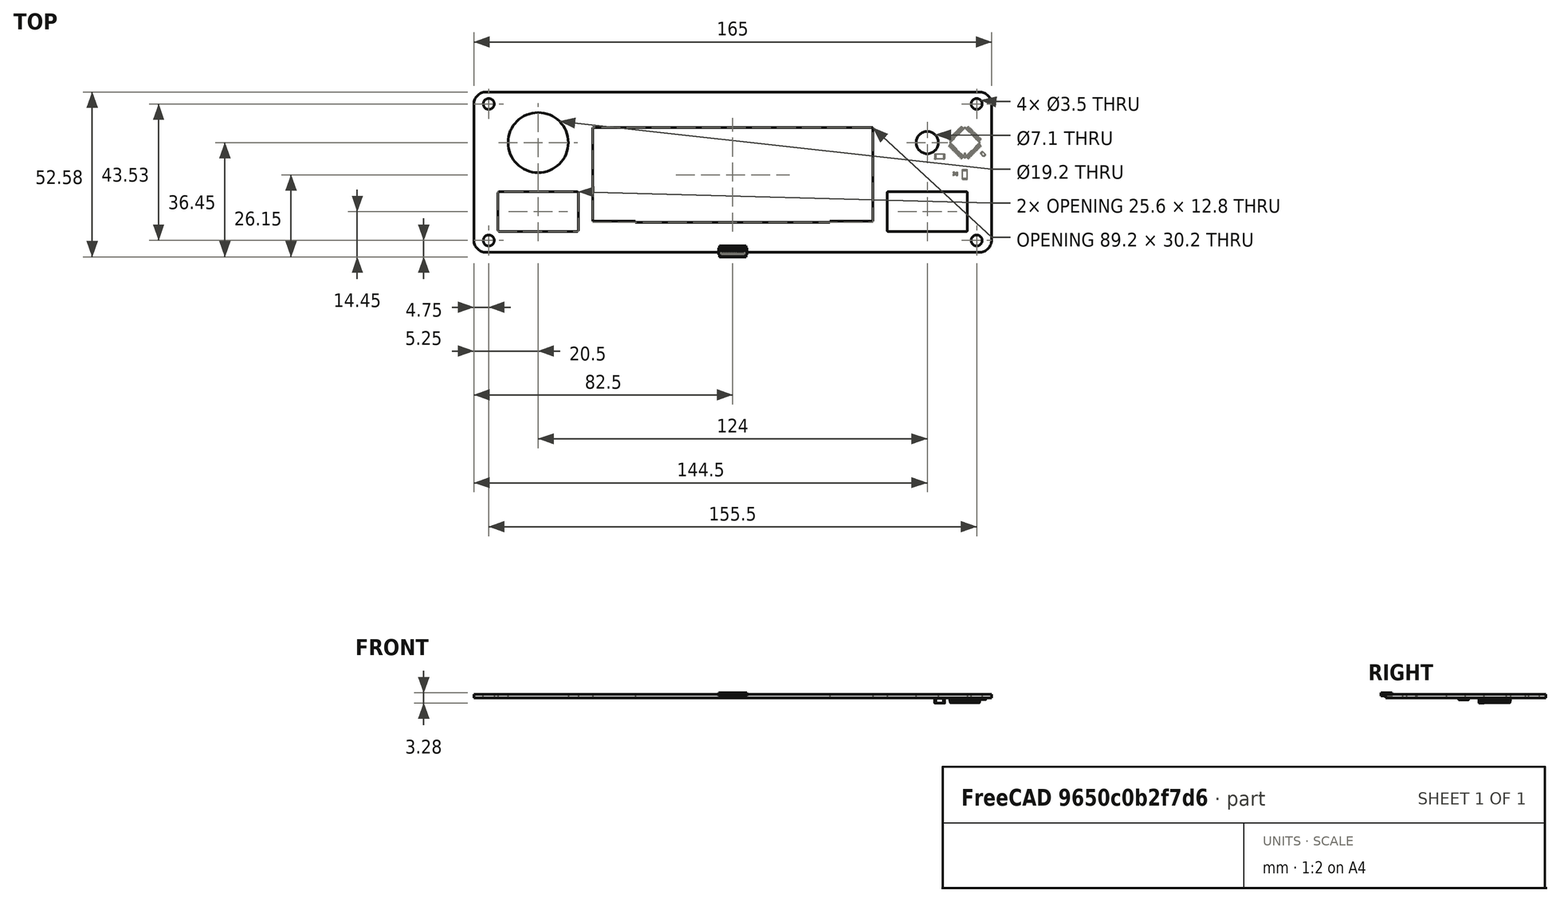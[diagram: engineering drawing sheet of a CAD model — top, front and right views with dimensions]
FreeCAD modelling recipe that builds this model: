
FCSTD DOCUMENT  (FreeCAD 0.19R)
Label: ss_frontpanel_outer_plate-3d
License: All rights reserved
LicenseURL: http://en.wikipedia.org/wiki/All_rights_reserved
objects: App::Link×30, Part::Feature×27, App::Part×5, PartDesign::CoordinateSystem×1, Sketcher::SketchObject×1
note: 29 computed .brp shape members not serialized (recipe doc carries the construction recipe); baked Part::Feature solids carry a one-line shape summary decoded from their .brp

FEATURE [PartDesign::CoordinateSystem] Local_CS_ea1d
  AttacherType = Attacher::AttachEngine3D
FEATURE [Part::Feature] Pcb_ea1d
  Placement = pos=(-150,100,0) rot=(0,0,1;0rad)
  shape: bbox 165 x 51.13 x 1.2 mm, 40 faces (baked)
FEATURE [Sketcher::SketchObject] PCB_Sketch_ea1d
  FullyConstrained = false
  sketch-geometry (8):
    g0: LineSegment StartX=-78.61 StartY=51.13 StartZ=0 EndX=78.61 EndY=51.13 EndZ=0
    g1: LineSegment StartX=82.5 StartY=47.24 StartZ=0 EndX=82.5 EndY=3.89 EndZ=0
    g2: LineSegment StartX=78.61 StartY=1.3e-15 StartZ=0 EndX=-78.61 EndY=-5.3e-15 EndZ=0
    g3: LineSegment StartX=-82.5 StartY=3.89 StartZ=0 EndX=-82.5 EndY=47.24 EndZ=0
    g4: ArcOfCircle CenterX=78.61 CenterY=47.24 CenterZ=0 NormalX=0 NormalY=0 NormalZ=-1 AngleXU=1.5708 Radius=3.89 StartAngle=0 EndAngle=1.5708
    g5: ArcOfCircle CenterX=-78.61 CenterY=47.24 CenterZ=0 NormalX=0 NormalY=0 NormalZ=-1 AngleXU=3.32483e-07 Radius=3.89 StartAngle=0 EndAngle=1.5708
    g6: ArcOfCircle CenterX=78.61 CenterY=3.89 CenterZ=0 NormalX=0 NormalY=0 NormalZ=-1 AngleXU=-3.14159 Radius=3.89 StartAngle=0 EndAngle=1.5708
    g7: ArcOfCircle CenterX=-78.61 CenterY=3.89 CenterZ=0 NormalX=0 NormalY=0 NormalZ=-1 AngleXU=-1.5708 Radius=3.89 StartAngle=0 EndAngle=1.5708
  constraints (8):
    c: Coincident(g3,g7)
    c: Coincident(g3,g5)
    c: Coincident(g2,g7)
    c: Coincident(g0,g5)
    c: Coincident(g2,g6)
    c: Coincident(g0,g4)
    c: Coincident(g1,g6)
    c: Coincident(g1,g4)
FEATURE [Part::Feature] Shape  label="C1_C_0402_1005Metric_00005f291953"
  Placement = pos=(70.5,25.1,-1.2) rot=(0.707107,-0.707107,0;3.14159rad)
  shape: bbox 0.5 x 1 x 0.5 mm, 28 faces (baked)
FEATURE [App::Link] C1_C_0402_1005Metric_00005f291953_ln_  label="C3_C_0402_1005Metric_00005f291971"
  LinkPlacement = pos=(70.6,21,-1.2) rot=(0.707107,0.707107,0;3.14159rad)
  LinkedObject = -> Shape
  Placement = pos=(70.6,21,-1.2) rot=(0.707107,0.707107,0;3.14159rad)
FEATURE [Part::Feature] Shape001  label="C6_C_1206_3216Metric_00005f2919ae"
  Placement = pos=(65.95,30.6,-1.2) rot=(1,0,0;3.14159rad)
  shape: bbox 3.2 x 1.6 x 1.6 mm, 28 faces (baked)
FEATURE [App::Link] C6_C_1206_3216Metric_00005f2919ae_ln_  label="C7_C_1206_3216Metric_00005f2919bf"
  LinkPlacement = pos=(61.3,45.45,-1.2) rot=(0.707107,0.707107,0;3.14159rad)
  LinkedObject = -> Shape001
  Placement = pos=(61.3,45.45,-1.2) rot=(0.707107,0.707107,0;3.14159rad)
FEATURE [App::Link] C6_C_1206_3216Metric_00005f2919ae_ln_001  label="C8_C_1206_3216Metric_00005f2919d0"
  LinkPlacement = pos=(64.3,45.5,-1.2) rot=(0.707107,0.707107,0;3.14159rad)
  LinkedObject = -> Shape001
  Placement = pos=(64.3,45.5,-1.2) rot=(0.707107,0.707107,0;3.14159rad)
FEATURE [App::Link] C6_C_1206_3216Metric_00005f2919ae_ln_002  label="C9_C_1206_3216Metric_00005f2919e1"
  LinkPlacement = pos=(72.9,45,-1.2) rot=(0,1,0;3.14159rad)
  LinkedObject = -> Shape001
  Placement = pos=(72.9,45,-1.2) rot=(0,1,0;3.14159rad)
FEATURE [App::Link] C1_C_0402_1005Metric_00005f291953_ln_001  label="C12_C_0402_1005Metric_00005f291a12"
  LinkPlacement = pos=(69,31.4,-1.2) rot=(0.707107,-0.707107,0;3.14159rad)
  LinkedObject = -> Shape
  Placement = pos=(69,31.4,-1.2) rot=(0.707107,-0.707107,0;3.14159rad)
FEATURE [App::Link] C1_C_0402_1005Metric_00005f291953_ln_002  label="C13_C_0402_1005Metric_00005f291a21"
  LinkPlacement = pos=(76.25,29.25,-1.2) rot=(0.92388,0.382683,0;3.14159rad)
  LinkedObject = -> Shape
  Placement = pos=(76.25,29.25,-1.2) rot=(0.92388,0.382683,0;3.14159rad)
FEATURE [App::Link] C1_C_0402_1005Metric_00005f291953_ln_003  label="C15_C_0402_1005Metric_00005f291a3f"
  LinkPlacement = pos=(73.2,40.9,-1.2) rot=(0.382683,0.92388,0;3.14159rad)
  LinkedObject = -> Shape
  Placement = pos=(73.2,40.9,-1.2) rot=(0.382683,0.92388,0;3.14159rad)
FEATURE [App::Link] C1_C_0402_1005Metric_00005f291953_ln_004  label="C17_C_0402_1005Metric_00005f291a5f"
  LinkPlacement = pos=(77,28.5,-1.2) rot=(0.92388,0.382683,0;3.14159rad)
  LinkedObject = -> Shape
  Placement = pos=(77,28.5,-1.2) rot=(0.92388,0.382683,0;3.14159rad)
FEATURE [Part::Feature] Shape002  label="R1_R_0402_1005Metric_00005f291bf3"
  Placement = pos=(71.4,25.1,-1.2) rot=(0.707107,0.707107,0;3.14159rad)
  shape: bbox 0.5 x 1 x 0.35 mm, 26 faces (baked)
FEATURE [App::Link] R1_R_0402_1005Metric_00005f291bf3_ln_  label="R2_R_0402_1005Metric_00005f291c02"
  LinkPlacement = pos=(70.2,40.15,-1.2) rot=(0.92388,-0.382683,0;3.14159rad)
  LinkedObject = -> Shape002
  Placement = pos=(70.2,40.15,-1.2) rot=(0.92388,-0.382683,0;3.14159rad)
FEATURE [App::Link] R1_R_0402_1005Metric_00005f291bf3_ln_001  label="R6_R_0402_1005Metric_00005f291c3e"
  LinkPlacement = pos=(79.1,39.2,-1.2) rot=(-0.382683,0.92388,0;3.14159rad)
  LinkedObject = -> Shape002
  Placement = pos=(79.1,39.2,-1.2) rot=(-0.382683,0.92388,0;3.14159rad)
FEATURE [Part::Feature] Shape003  label="R8_R_0603_1608Metric_00005f291c5c"
  Placement = pos=(79.8,31.35,-1.2) rot=(0.382683,0.92388,0;3.14159rad)
  shape: bbox 1.697 x 1.697 x 0.45 mm, 26 faces (baked)
FEATURE [App::Link] R1_R_0402_1005Metric_00005f291bf3_ln_002  label="R9_R_0402_1005Metric_00005f291c6b"
  LinkPlacement = pos=(69,39,-1.2) rot=(0.92388,-0.382683,0;3.14159rad)
  LinkedObject = -> Shape002
  Placement = pos=(69,39,-1.2) rot=(0.92388,-0.382683,0;3.14159rad)
FEATURE [Part::Feature] Shape004  label="R12_R_1206_3216Metric_00005f291c98"
  Placement = pos=(74,24.9,-1.2) rot=(0.707107,0.707107,0;3.14159rad)
  shape: bbox 1.6 x 3.2 x 0.55 mm, 26 faces (baked)
FEATURE [Part::Feature] Part__Feature  label="6871xx182122_Pad"
  Placement = pos=(4.195,-0.75,-0.03) rot=(0,0,1;0rad)
  shape: bbox 0.15 x 1.65 x 0.95 mm, 18 faces (baked)
FEATURE [Part::Feature] Part__Feature001  label="6871xx182122_Pad001"
  Placement = pos=(-4.195,-0.75,-0.03) rot=(0,0,1;0rad)
  shape: bbox 0.15 x 1.65 x 0.95 mm, 18 faces (baked)
FEATURE [Part::Feature] Part__Feature002  label="6871xx182122_Pin"
  Placement = pos=(-3.25,0.34,-0.18) rot=(0,0,1;0rad)
  shape: bbox 0.17 x 2.8 x 0.9883 mm, 28 faces (baked)
FEATURE [Part::Feature] Part__Feature003  label="6871xx182122_Pin001"
  Placement = pos=(-2.75,0.34,-0.18) rot=(0,0,1;0rad)
  shape: bbox 0.17 x 2.8 x 0.9883 mm, 28 faces (baked)
FEATURE [Part::Feature] Part__Feature004  label="6871xx182122_Pin002"
  Placement = pos=(-2.25,0.34,-0.18) rot=(0,0,1;0rad)
  shape: bbox 0.17 x 2.8 x 0.9883 mm, 28 faces (baked)
FEATURE [Part::Feature] Part__Feature005  label="6871xx182122_Pin003"
  Placement = pos=(-1.75,0.34,-0.18) rot=(0,0,1;0rad)
  shape: bbox 0.17 x 2.8 x 0.9883 mm, 28 faces (baked)
FEATURE [Part::Feature] Part__Feature006  label="6871xx182122_Pin004"
  Placement = pos=(-1.25,0.34,-0.18) rot=(0,0,1;0rad)
  shape: bbox 0.17 x 2.8 x 0.9883 mm, 28 faces (baked)
FEATURE [Part::Feature] Part__Feature007  label="6871xx182122_Pin005"
  Placement = pos=(-0.75,0.34,-0.18) rot=(0,0,1;0rad)
  shape: bbox 0.17 x 2.8 x 0.9883 mm, 28 faces (baked)
FEATURE [Part::Feature] Part__Feature008  label="6871xx182122_Pin006"
  Placement = pos=(-0.25,0.34,-0.18) rot=(0,0,1;0rad)
  shape: bbox 0.17 x 2.8 x 0.9883 mm, 28 faces (baked)
FEATURE [Part::Feature] Part__Feature009  label="6871xx182122_Pin007"
  Placement = pos=(0.25,0.34,-0.18) rot=(0,0,1;0rad)
  shape: bbox 0.17 x 2.8 x 0.9883 mm, 28 faces (baked)
FEATURE [Part::Feature] Part__Feature010  label="6871xx182122_Pin008"
  Placement = pos=(0.75,0.34,-0.18) rot=(0,0,1;0rad)
  shape: bbox 0.17 x 2.8 x 0.9883 mm, 28 faces (baked)
FEATURE [Part::Feature] Part__Feature011  label="6871xx182122_Pin009"
  Placement = pos=(1.25,0.34,-0.18) rot=(0,0,1;0rad)
  shape: bbox 0.17 x 2.8 x 0.9883 mm, 28 faces (baked)
FEATURE [Part::Feature] Part__Feature012  label="6871xx182122_Pin010"
  Placement = pos=(1.75,0.34,-0.18) rot=(0,0,1;0rad)
  shape: bbox 0.17 x 2.8 x 0.9883 mm, 28 faces (baked)
FEATURE [Part::Feature] Part__Feature013  label="6871xx182122_Pin011"
  Placement = pos=(2.25,0.34,-0.18) rot=(0,0,1;0rad)
  shape: bbox 0.17 x 2.8 x 0.9883 mm, 28 faces (baked)
FEATURE [Part::Feature] Part__Feature014  label="6871xx182122_Pin012"
  Placement = pos=(2.75,0.34,-0.18) rot=(0,0,1;0rad)
  shape: bbox 0.17 x 2.8 x 0.9883 mm, 28 faces (baked)
FEATURE [Part::Feature] Part__Feature015  label="6871xx182122_Pin013"
  Placement = pos=(3.25,0.34,-0.18) rot=(0,0,1;0rad)
  shape: bbox 0.17 x 2.8 x 0.9883 mm, 28 faces (baked)
FEATURE [Part::Feature] Part__Feature016  label="687114182122"
  shape: bbox 9 x 2.9 x 0.96 mm, 303 faces (baked)
FEATURE [Part::Feature] Part__Feature017  label="687114182122_Actuator"
  Placement = pos=(-3e-16,1.325,0.145) rot=(0,0.707107,0.707107;3.14159rad)
  shape: bbox 8.5 x 1.45 x 0.65 mm, 62 faces (baked)
FEATURE [App::Part] Assem1  label="J2_Assem1_00005f296a69"
  Group = -> [Part__Feature,Part__Feature001,Part__Feature002,Part__Feature003,Part__Feature004,Part__Feature005,Part__Feature006,Part__Feature007,Part__Feature008,Part__Feature009,Part__Feature010,Part__Feature011,Part__Feature012,Part__Feature013,Part__Feature014,Part__Feature015,Part__Feature016,Part__Feature017]
  Origin = -> Origin008
  Placement = pos=(67.15,24.5,-1.7) rot=(0.707107,0.707107,0;3.14159rad)
FEATURE [App::Link] R1_R_0402_1005Metric_00005f291bf3_ln_003  label="R17_R_0402_1005Metric_00005f29c17f"
  LinkPlacement = pos=(64,21.75,-1.2) rot=(0.707107,-0.707107,0;3.14159rad)
  LinkedObject = -> Shape002
  Placement = pos=(64,21.75,-1.2) rot=(0.707107,-0.707107,0;3.14159rad)
FEATURE [App::Link] R8_R_0603_1608Metric_00005f291c5c_ln_  label="R11_R_0603_1608Metric_00005f2a94d4"
  LinkPlacement = pos=(77.55,40.95,-1.2) rot=(-0.382683,0.92388,0;3.14159rad)
  LinkedObject = -> Shape003
  Placement = pos=(77.55,40.95,-1.2) rot=(-0.382683,0.92388,0;3.14159rad)
FEATURE [App::Link] R1_R_0402_1005Metric_00005f291bf3_ln_004  label="R5_R_0402_1005Metric_00005f2abe7b"
  LinkPlacement = pos=(67.5,37.5,-1.2) rot=(0.92388,-0.382683,0;3.14159rad)
  LinkedObject = -> Shape002
  Placement = pos=(67.5,37.5,-1.2) rot=(0.92388,-0.382683,0;3.14159rad)
FEATURE [App::Link] C6_C_1206_3216Metric_00005f2919ae_ln_003  label="C4_C_1206_3216Metric_00005f2add4c"
  LinkPlacement = pos=(73.4,42.8,-1.2) rot=(0,1,0;3.14159rad)
  LinkedObject = -> Shape001
  Placement = pos=(73.4,42.8,-1.2) rot=(0,1,0;3.14159rad)
FEATURE [App::Link] R1_R_0402_1005Metric_00005f291bf3_ln_005  label="R3_R_0402_1005Metric_00005f2b3c71"
  LinkPlacement = pos=(67.2,35.1,-1.2) rot=(0.92388,-0.382683,0;3.14159rad)
  LinkedObject = -> Shape002
  Placement = pos=(67.2,35.1,-1.2) rot=(0.92388,-0.382683,0;3.14159rad)
FEATURE [App::Link] R1_R_0402_1005Metric_00005f291bf3_ln_006  label="R4_R_0402_1005Metric_00005f2b3c9b"
  LinkPlacement = pos=(67.2,32.5,-1.2) rot=(1,0,0;3.14159rad)
  LinkedObject = -> Shape002
  Placement = pos=(67.2,32.5,-1.2) rot=(1,0,0;3.14159rad)
FEATURE [App::Link] R1_R_0402_1005Metric_00005f291bf3_ln_007  label="R7_R_0402_1005Metric_00005f2b3cc5"
  LinkPlacement = pos=(67.9,35.8,-1.2) rot=(0.92388,-0.382683,0;3.14159rad)
  LinkedObject = -> Shape002
  Placement = pos=(67.9,35.8,-1.2) rot=(0.92388,-0.382683,0;3.14159rad)
FEATURE [App::Link] C6_C_1206_3216Metric_00005f2919ae_ln_004  label="C10_C_1206_3216Metric_00005f2be6f3"
  LinkPlacement = pos=(78.15,27.45,-1.2) rot=(-0.382683,0.92388,0;3.14159rad)
  LinkedObject = -> Shape001
  Placement = pos=(78.15,27.45,-1.2) rot=(-0.382683,0.92388,0;3.14159rad)
FEATURE [App::Link] R1_R_0402_1005Metric_00005f291bf3_ln_008  label="R10_R_0402_1005Metric_00005f2bfece"
  LinkPlacement = pos=(79.6,37.75,-1.2) rot=(0.382683,0.92388,0;3.14159rad)
  LinkedObject = -> Shape002
  Placement = pos=(79.6,37.75,-1.2) rot=(0.382683,0.92388,0;3.14159rad)
FEATURE [App::Link] R1_R_0402_1005Metric_00005f291bf3_ln_009  label="R13_R_0402_1005Metric_00005f2bff15"
  LinkPlacement = pos=(80,33.6,-1.2) rot=(0.707107,0.707107,0;3.14159rad)
  LinkedObject = -> Shape002
  Placement = pos=(80,33.6,-1.2) rot=(0.707107,0.707107,0;3.14159rad)
FEATURE [App::Link] C1_C_0402_1005Metric_00005f291953_ln_005  label="C2_C_0402_1005Metric_00005f2d5a5f"
  LinkPlacement = pos=(70.5,27,-1.2) rot=(0.707107,-0.707107,0;3.14159rad)
  LinkedObject = -> Shape
  Placement = pos=(70.5,27,-1.2) rot=(0.707107,-0.707107,0;3.14159rad)
FEATURE [App::Link] R8_R_0603_1608Metric_00005f291c5c_ln_001  label="R18_R_0603_1608Metric_00005f2db44b"
  LinkPlacement = pos=(76.4,13.15,-1.2) rot=(1,0,0;3.14159rad)
  LinkedObject = -> Shape003
  Placement = pos=(76.4,13.15,-1.2) rot=(1,0,0;3.14159rad)
FEATURE [App::Link] R8_R_0603_1608Metric_00005f291c5c_ln_002  label="R19_R_0603_1608Metric_00005f2db5fc"
  LinkPlacement = pos=(76.3,20.8,-1.2) rot=(1,0,0;3.14159rad)
  LinkedObject = -> Shape003
  Placement = pos=(76.3,20.8,-1.2) rot=(1,0,0;3.14159rad)
FEATURE [App::Link] R8_R_0603_1608Metric_00005f291c5c_ln_003  label="R14_R_0603_1608Metric_00005f2fc193"
  LinkPlacement = pos=(74.05,27.95,-1.2) rot=(1,0,0;3.14159rad)
  LinkedObject = -> Shape003
  Placement = pos=(74.05,27.95,-1.2) rot=(1,0,0;3.14159rad)
FEATURE [App::Link] C1_C_0402_1005Metric_00005f291953_ln_006  label="C14_C_0402_1005Metric_00005f307618"
  LinkPlacement = pos=(80,35.45,-1.2) rot=(0.707107,-0.707107,0;3.14159rad)
  LinkedObject = -> Shape
  Placement = pos=(80,35.45,-1.2) rot=(0.707107,-0.707107,0;3.14159rad)
FEATURE [App::Link] R1_R_0402_1005Metric_00005f291bf3_ln_010  label="R20_R_0402_1005Metric_00005f31142d"
  LinkPlacement = pos=(72.1,27.8,-1.2) rot=(0.707107,-0.707107,0;3.14159rad)
  LinkedObject = -> Shape002
  Placement = pos=(72.1,27.8,-1.2) rot=(0.707107,-0.707107,0;3.14159rad)
FEATURE [Part::Feature] Shape005  label="U1_LQFP_48_7x7mm_P05mm_00005f312d9e"
  Placement = pos=(74,35,-1.2) rot=(0.92388,0.382683,0;3.14159rad)
  shape: bbox 10.41 x 10.41 x 1.5 mm, 764 faces (baked)
FEATURE [App::Link] R1_R_0402_1005Metric_00005f291bf3_ln_011  label="R15_R_0402_1005Metric_00005f35601a"
  LinkPlacement = pos=(60.5,21.25,-1.2) rot=(1,0,0;3.14159rad)
  LinkedObject = -> Shape002
  Placement = pos=(60.5,21.25,-1.2) rot=(1,0,0;3.14159rad)
FEATURE [App::Link] R1_R_0402_1005Metric_00005f291bf3_ln_012  label="R16_R_0402_1005Metric_00005f356029"
  LinkPlacement = pos=(63,21.75,-1.2) rot=(0.707107,0.707107,0;3.14159rad)
  LinkedObject = -> Shape002
  Placement = pos=(63,21.75,-1.2) rot=(0.707107,0.707107,0;3.14159rad)
FEATURE [App::Link] R1_R_0402_1005Metric_00005f291bf3_ln_013  label="R21_R_0402_1005Metric_00005f3560a2"
  LinkPlacement = pos=(60.5,22.25,-1.2) rot=(1,0,0;3.14159rad)
  LinkedObject = -> Shape002
  Placement = pos=(60.5,22.25,-1.2) rot=(1,0,0;3.14159rad)
FEATURE [App::Part] Bot_ea1d
  Group = -> [Shape,C1_C_0402_1005Metric_00005f291953_ln_,Shape001,C6_C_1206_3216Metric_00005f2919ae_ln_,C6_C_1206_3216Metric_00005f2919ae_ln_001,C6_C_1206_3216Metric_00005f2919ae_ln_002,C1_C_0402_1005Metric_00005f291953_ln_001,C1_C_0402_1005Metric_00005f291953_ln_002,C1_C_0402_1005Metric_00005f291953_ln_003,C1_C_0402_1005Metric_00005f291953_ln_004,Shape002,R1_R_0402_1005Metric_00005f291bf3_ln_,+25 more]
  Origin = -> Origin004
FEATURE [App::Part] Step_Models_ea1d
  Group = -> [Bot_ea1d]
  Origin = -> Origin002
FEATURE [Part::Feature] botSilks_9593
  Placement = pos=(-150,100,-1.27) rot=(0,0,1;0rad)
  shape: bbox 161.1 x 49.31 x 2e-07 mm, 235 faces, 0 solids (baked)
FEATURE [Part::Feature] topSilks_9847
  Placement = pos=(-150,100,0.07) rot=(0,0,1;0rad)
FEATURE [App::Part] Board_Geoms_ea1d
  Group = -> [Local_CS_ea1d,Pcb_ea1d,PCB_Sketch_ea1d,botSilks_9593,topSilks_9847]
  Origin = -> Origin
FEATURE [App::Part] Board_ea1d  label="ss_frontpanel_outer_plate"
  Group = -> [Board_Geoms_ea1d,Step_Models_ea1d]
  Origin = -> Origin001
